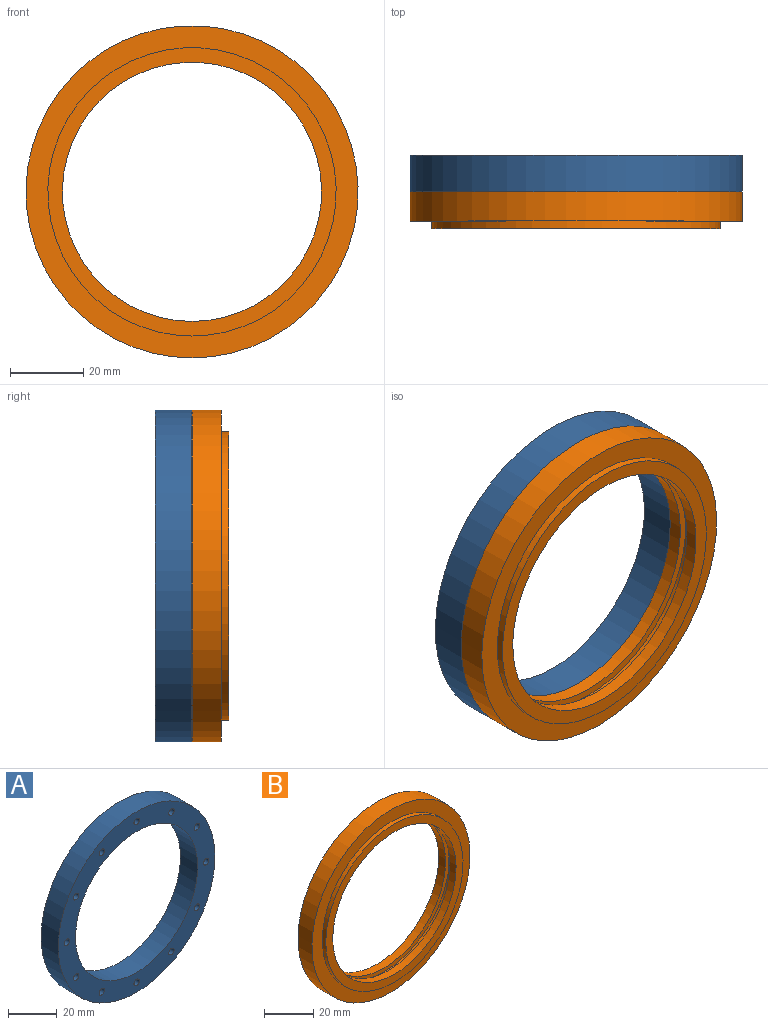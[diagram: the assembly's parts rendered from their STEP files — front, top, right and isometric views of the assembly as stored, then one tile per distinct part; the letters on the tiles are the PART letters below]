
ASSEMBLY  parts=2 mates=1
PART A: 28 faces, bbox 91x10x91 mm
  f0: plane 91x91mm, normal (0,-1,0), area 2454.1mm2, adj f1,f3,f4,f6,f8,f10,f12,f14
  f1: cylinder r=35.5mm len=71mm, axis (0,-1,0), area 2230.5mm2, adj f0,f2
  f2: plane 91x91mm, normal (0,1,0), area 2544.7mm2, adj f1,f3
  f3: cylinder r=45.5mm len=91mm, axis (0,-1,0), area 2858.8mm2, adj f0,f2
  f4: cylinder r=1.55mm len=4.5mm, axis (0,-1,0), area 43.8mm2, adj f0,f5
  f5: plane 3.1x3.1mm, normal (0,-1,0), area 7.5mm2, adj f4
  f6: cylinder r=1.55mm len=4.5mm, axis (0,-1,0), area 43.8mm2, adj f0,f7
  f7: plane 3.1x3.1mm, normal (0,-1,0), area 7.5mm2, adj f6
  f8: cylinder r=1.55mm len=4.5mm, axis (0,-1,0), area 43.8mm2, adj f0,f9
  f9: plane 3.1x3.1mm, normal (0,-1,0), area 7.5mm2, adj f8
  f10: cylinder r=1.55mm len=4.5mm, axis (0,-1,0), area 43.8mm2, adj f0,f11
  f11: plane 3.1x3.1mm, normal (0,-1,0), area 7.5mm2, adj f10
  f12: cylinder r=1.55mm len=4.5mm, axis (0,-1,0), area 43.8mm2, adj f0,f13
  f13: plane 3.1x3.1mm, normal (0,-1,0), area 7.5mm2, adj f12
  f14: cylinder r=1.55mm len=4.5mm, axis (0,-1,0), area 43.8mm2, adj f0,f15
  f15: plane 3.1x3.1mm, normal (0,-1,0), area 7.5mm2, adj f14
  f16: cylinder r=1.55mm len=4.5mm, axis (0,-1,0), area 43.8mm2, adj f0,f17
  f17: plane 3.1x3.1mm, normal (0,-1,0), area 7.5mm2, adj f16
  f18: cylinder r=1.55mm len=4.5mm, axis (0,-1,0), area 43.8mm2, adj f0,f19
  f19: plane 3.1x3.1mm, normal (0,-1,0), area 7.5mm2, adj f18
  f20: cylinder r=1.55mm len=4.5mm, axis (0,-1,0), area 43.8mm2, adj f0,f21
  f21: plane 3.1x3.1mm, normal (0,-1,0), area 7.5mm2, adj f20
  f22: cylinder r=1.55mm len=4.5mm, axis (0,-1,0), area 43.8mm2, adj f0,f23
  f23: plane 3.1x3.1mm, normal (0,-1,0), area 7.5mm2, adj f22
  f24: cylinder r=1.55mm len=4.5mm, axis (0,-1,0), area 43.8mm2, adj f0,f25
  f25: plane 3.1x3.1mm, normal (0,-1,0), area 7.5mm2, adj f24
  f26: cylinder r=1.55mm len=4.5mm, axis (0,-1,0), area 43.8mm2, adj f0,f27
  f27: plane 3.1x3.1mm, normal (0,-1,0), area 7.5mm2, adj f26
PART B: 34 faces, bbox 91x10x91 mm
  f0: plane 91x91mm, normal (0,1,0), area 2454.1mm2, adj f1,f9,f10,f12,f14,f16,f18,f20
  f1: cylinder r=45.5mm len=91mm, axis (0,-1,0), area 2287.1mm2, adj f0,f2
  f2: plane 91x91mm, normal (0,-1,0), area 1602.2mm2, adj f1,f3
  f3: cylinder r=39.5mm len=79mm, axis (0,-1,0), area 496.4mm2, adj f2,f4
  f4: plane 79x79mm, normal (0,-1,0), area 942.5mm2, adj f3,f5
  f5: cylinder r=35.5mm len=71mm, axis (0,-1,0), area 798.9mm2, adj f4,f6
  f6: plane 75x75mm, normal (0,1,0), area 458.7mm2, adj f5,f7
  f7: cylinder r=37.5mm len=75mm, axis (0,-1,0), area 589mm2, adj f6,f8
  f8: plane 75x75mm, normal (0,-1,0), area 458.7mm2, adj f7,f9
  f9: cylinder r=35.5mm len=71mm, axis (0,-1,0), area 874mm2, adj f0,f8
  f10: cylinder r=1.55mm len=4.5mm, axis (0,1,0), area 43.8mm2, adj f0,f11
  f11: plane 3.1x3.1mm, normal (0,1,0), area 7.5mm2, adj f10
  f12: cylinder r=1.55mm len=4.5mm, axis (0,1,0), area 43.8mm2, adj f0,f13
  f13: plane 3.1x3.1mm, normal (0,1,0), area 7.5mm2, adj f12
  f14: cylinder r=1.55mm len=4.5mm, axis (0,1,0), area 43.8mm2, adj f0,f15
  f15: plane 3.1x3.1mm, normal (0,1,0), area 7.5mm2, adj f14
  f16: cylinder r=1.55mm len=4.5mm, axis (0,1,0), area 43.8mm2, adj f0,f17
  f17: plane 3.1x3.1mm, normal (0,1,0), area 7.5mm2, adj f16
  f18: cylinder r=1.55mm len=4.5mm, axis (0,1,0), area 43.8mm2, adj f0,f19
  f19: plane 3.1x3.1mm, normal (0,1,0), area 7.5mm2, adj f18
  f20: cylinder r=1.55mm len=4.5mm, axis (0,1,0), area 43.8mm2, adj f0,f21
  f21: plane 3.1x3.1mm, normal (0,1,0), area 7.5mm2, adj f20
  f22: cylinder r=1.55mm len=4.5mm, axis (0,1,0), area 43.8mm2, adj f0,f23
  f23: plane 3.1x3.1mm, normal (0,1,0), area 7.5mm2, adj f22
  f24: cylinder r=1.55mm len=4.5mm, axis (0,1,0), area 43.8mm2, adj f0,f25
  f25: plane 3.1x3.1mm, normal (0,1,0), area 7.5mm2, adj f24
  f26: cylinder r=1.55mm len=4.5mm, axis (0,1,0), area 43.8mm2, adj f0,f27
  f27: plane 3.1x3.1mm, normal (0,1,0), area 7.5mm2, adj f26
  f28: cylinder r=1.55mm len=4.5mm, axis (0,1,0), area 43.8mm2, adj f0,f29
  f29: plane 3.1x3.1mm, normal (0,1,0), area 7.5mm2, adj f28
  f30: cylinder r=1.55mm len=4.5mm, axis (0,1,0), area 43.8mm2, adj f0,f31
  f31: plane 3.1x3.1mm, normal (0,1,0), area 7.5mm2, adj f30
  f32: cylinder r=1.55mm len=4.5mm, axis (0,1,0), area 43.8mm2, adj f0,f33
  f33: plane 3.1x3.1mm, normal (0,1,0), area 7.5mm2, adj f32
PLACE A t=(87.99,-100.43,196.16)mm
PLACE B t=(87.99,-61.21,196.16)mm
MATE fastened B.f32 <-> A.f26  axis (0,1,0) through (87.99,-83.33,236.66)mm
